# Revit family: Faucet_Contemporary_Neorest-II_TL993SE_TOTO
name_source: partatom
category: Plumbing Fixtures
revit_build: Autodesk Revit Architecture 2013 (Build: 20130531_2115(x64)
units: mm (PartAtom-declared; Revit-internal decimal feet)

## types (1)
- TL993SE
    04 CSI = 22 41 39
    95 CSI = 15416
    ADA Compliant = Yes
    Apparent Power = 96 VA
    Assembly Code = D2010
    CAD Drawing URL = http://assets.totousa.com
    CW Connection = Yes
    CWFU = 0
    Cold Water Connection NPT Radius = 1/4"
    Color Availability = #CP Polished Chrome
    Current = 1 A
    Default Elevation = 0"
    Depth = 7 7/8"
    Description = Electronic Deck-Mount Lavatory Faucet
    Finish = Metal - TOTO - Chrome - Polished
    Flow Pressure = 0.00 psi
    Flow Rate = 1.000 GPM
    Frequency = 60 Hz
    HW Connection = Yes
    HWFU = 0
    Height = 5 29/32"
    Hot Water Connection NPT Radius = 1/4"
    Manufacturer = TOTO USA, Inc.
    Manufacturer Fax = (770) 282-0002
    Model = TL993SE
    Number of Poles = 1
    Series = Neorest II
    Shipping Weight = 16.50 lb
    Spec Sheet URL = http://assets.totousa.com
    Style = Contemporary
    Subcategory = Faucets
    Toto BIM Number = BM-00235
    URL = http://www.totousa.com
    Vent Connection = No
    Voltage = 120 V
    WFU = 0
    Warranty = Three Year Limited Warranty
    Warranty URL = http://www.totousa.com
    Waste Connection = No
    Width = 1 31/32"

## geometry (parser evidence)
native form markers: Blend x30, Sweep x2
no freeform markers — native parametric forms only
